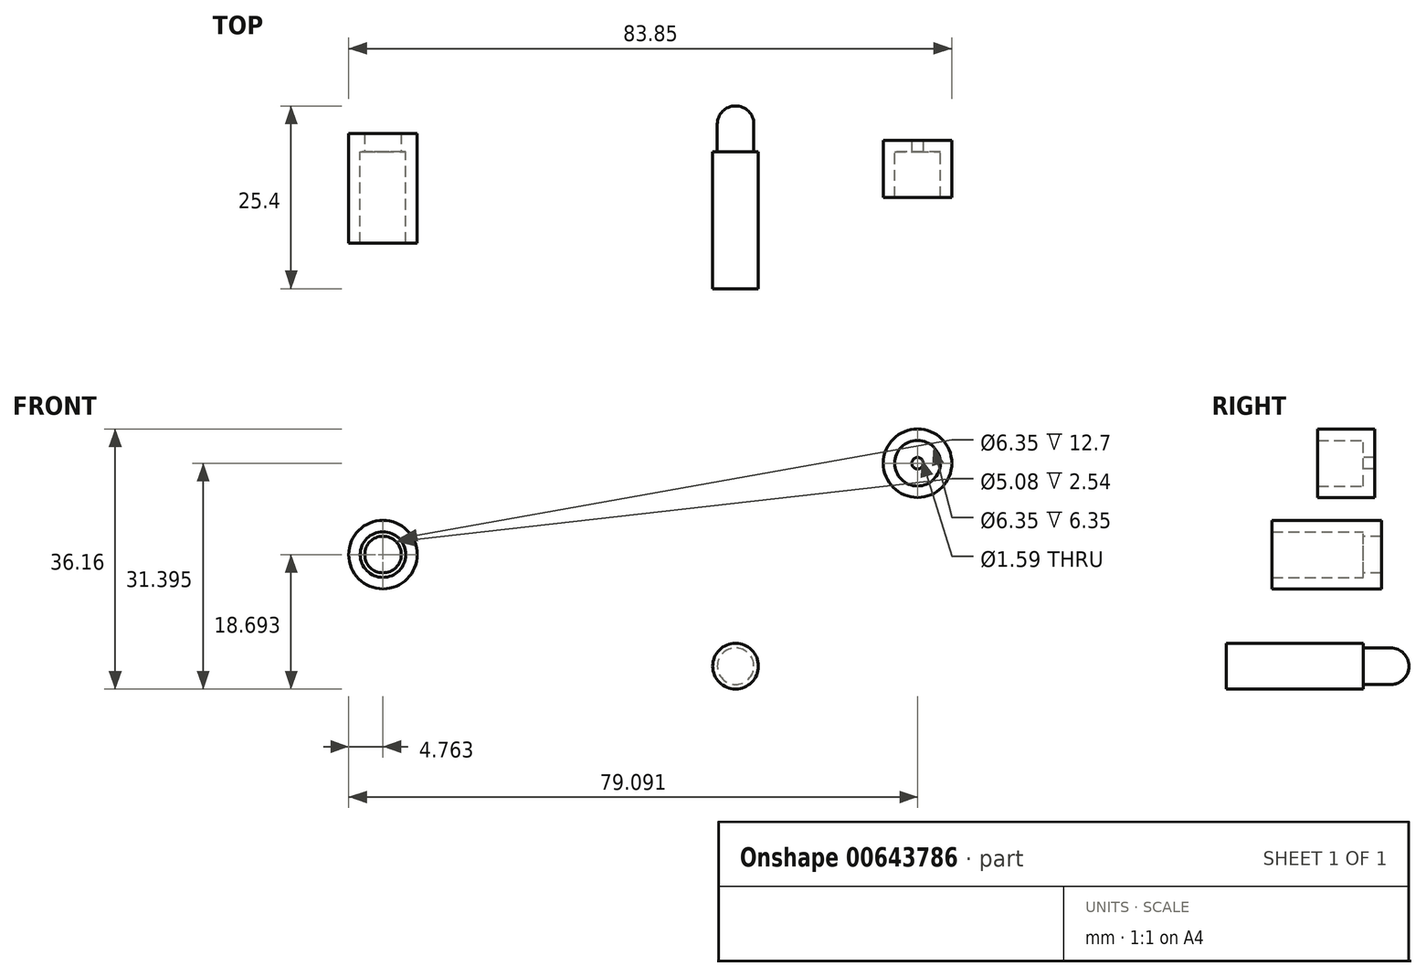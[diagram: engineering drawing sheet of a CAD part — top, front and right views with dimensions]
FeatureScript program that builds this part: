
annotation { "Feature Type Name" : "Feature", "Feature Type Description" : "" }
export const myFeature = defineFeature(function(context is Context, id is Id, definition is map)
    precondition{}
    {
        {
            var Q0;
            Q0=qCreatedBy(makeId("Front.planeOp"),FACE);
            var sketch = newSketch(context, id + "F0", { "sketchPlane" : qUnion([Q0])});
            skCircle(sketch, "E0", {"center": v(0, 0) * mm, "radius": 3.18 * mm});
            skCircle(sketch, "E1", {"center": v(0, 0) * mm, "radius": 2.54 * mm});
            skSolve(sketch);
        }
        {
            var Q0;
            Q0=makeQuery(id+"F0.imprint","IMPRINT",FACE,{"disambiguationData":[TD([[makeQuery(id+"F0.imprint","IMPRINT",EDGE,{"derivedFrom":sQuery(id+"F0.wireOp",EDGE,"E1")}),1.0]])]});
            var Q1;
            Q1=makeQuery(id+"F0.imprint","IMPRINT",FACE,{"disambiguationData":[TD([[makeQuery(id+"F0.imprint","IMPRINT",EDGE,{"derivedFrom":sQuery(id+"F0.wireOp",EDGE,"E0")}),1.0]])]});
            extrude(context, id + "F1", {"entities" : qUnion([Q0, Q1]), "depth" : 19.05 * mm, "offsetDistance" : 25.4 * mm});
        }
        {
            var Q0;
            Q0=makeQuery(id+"F0.imprint","IMPRINT",FACE,{"disambiguationData":[TD([[makeQuery(id+"F0.imprint","IMPRINT",EDGE,{"derivedFrom":sQuery(id+"F0.wireOp",EDGE,"E1")}),1.0]])]});
            extrude(context, id + "F2", {"entities" : qUnion([Q0]), "operationType" : NewBodyOperationType.ADD, "oppositeDirection" : true, "depth" : 6.35 * mm, "offsetDistance" : 25.4 * mm});
        }
        {
            var Q0;
            Q0=makeQuery(id+"F2.opExtrude","CAP_EDGE",EDGE,{"disambiguationData":[OSD([sQuery(id+"F0.wireOp",EDGE,"E1")])],"isStart":false});
            fillet(context, id + "F3", {"entities" : qUnion([Q0]), "radius" : 2.54 * mm, "tangentPropagation" : true, "allowEdgeOverflow" : false});
        }
        {
            var Q0;
            Q0=qCreatedBy(makeId("Front.planeOp"),FACE);
            var sketch = newSketch(context, id + "F4", { "sketchPlane" : qUnion([Q0])});
            skCircle(sketch, "E2", {"center": v(-49.03, 15.51) * mm, "radius": 4.76 * mm});
            skCircle(sketch, "E3", {"center": v(-49.03, 15.51) * mm, "radius": 3.18 * mm});
            skCircle(sketch, "E4", {"center": v(-49.03, 15.51) * mm, "radius": 2.54 * mm});
            skSolve(sketch);
        }
        {
            var Q0;
            Q0=makeQuery(id+"F4.imprint","IMPRINT",FACE,{"disambiguationData":[TD([[makeQuery(id+"F4.imprint","IMPRINT",EDGE,{"derivedFrom":sQuery(id+"F4.wireOp",EDGE,"E2")}),1.0]])]});
            extrude(context, id + "F5", {"entities" : qUnion([Q0]), "depth" : 12.7 * mm, "offsetDistance" : 25.4 * mm});
        }
        {
            var Q0;
            Q0=makeQuery(id+"F4.imprint","IMPRINT",FACE,{"disambiguationData":[TD([[makeQuery(id+"F4.imprint","IMPRINT",EDGE,{"derivedFrom":sQuery(id+"F4.wireOp",EDGE,"E3")}),1.0]])]});
            var Q1;
            Q1=makeQuery(id+"F4.imprint","IMPRINT",FACE,{"disambiguationData":[TD([[makeQuery(id+"F4.imprint","IMPRINT",EDGE,{"derivedFrom":sQuery(id+"F4.wireOp",EDGE,"E2")}),1.0]])]});
            extrude(context, id + "F6", {"entities" : qUnion([Q0, Q1]), "operationType" : NewBodyOperationType.ADD, "oppositeDirection" : true, "depth" : 2.54 * mm, "offsetDistance" : 25.4 * mm});
        }
        {
            var Q0;
            Q0=qCreatedBy(makeId("Front.planeOp"),FACE);
            var sketch = newSketch(context, id + "F7", { "sketchPlane" : qUnion([Q0])});
            skCircle(sketch, "E5", {"center": v(25.3, 28.22) * mm, "radius": 4.76 * mm});
            skCircle(sketch, "E6", {"center": v(25.3, 28.22) * mm, "radius": 3.18 * mm});
            skCircle(sketch, "E7", {"center": v(25.3, 28.22) * mm, "radius": 0.8 * mm});
            skSolve(sketch);
        }
        {
            var Q0;
            Q0=makeQuery(id+"F7.imprint","IMPRINT",FACE,{"disambiguationData":[TD([[makeQuery(id+"F7.imprint","IMPRINT",EDGE,{"derivedFrom":sQuery(id+"F7.wireOp",EDGE,"E5")}),1.0]])]});
            extrude(context, id + "F8", {"entities" : qUnion([Q0]), "depth" : 6.35 * mm, "offsetDistance" : 25.4 * mm});
        }
        {
            var Q0;
            Q0=makeQuery(id+"F7.imprint","IMPRINT",FACE,{"disambiguationData":[TD([[makeQuery(id+"F7.imprint","IMPRINT",EDGE,{"derivedFrom":sQuery(id+"F7.wireOp",EDGE,"E6")}),1.0]])]});
            var Q1;
            Q1=makeQuery(id+"F7.imprint","IMPRINT",FACE,{"disambiguationData":[TD([[makeQuery(id+"F7.imprint","IMPRINT",EDGE,{"derivedFrom":sQuery(id+"F7.wireOp",EDGE,"E5")}),1.0]])]});
            extrude(context, id + "F9", {"entities" : qUnion([Q0, Q1]), "operationType" : NewBodyOperationType.ADD, "oppositeDirection" : true, "depth" : 1.59 * mm, "offsetDistance" : 25.4 * mm});
        }
    });
